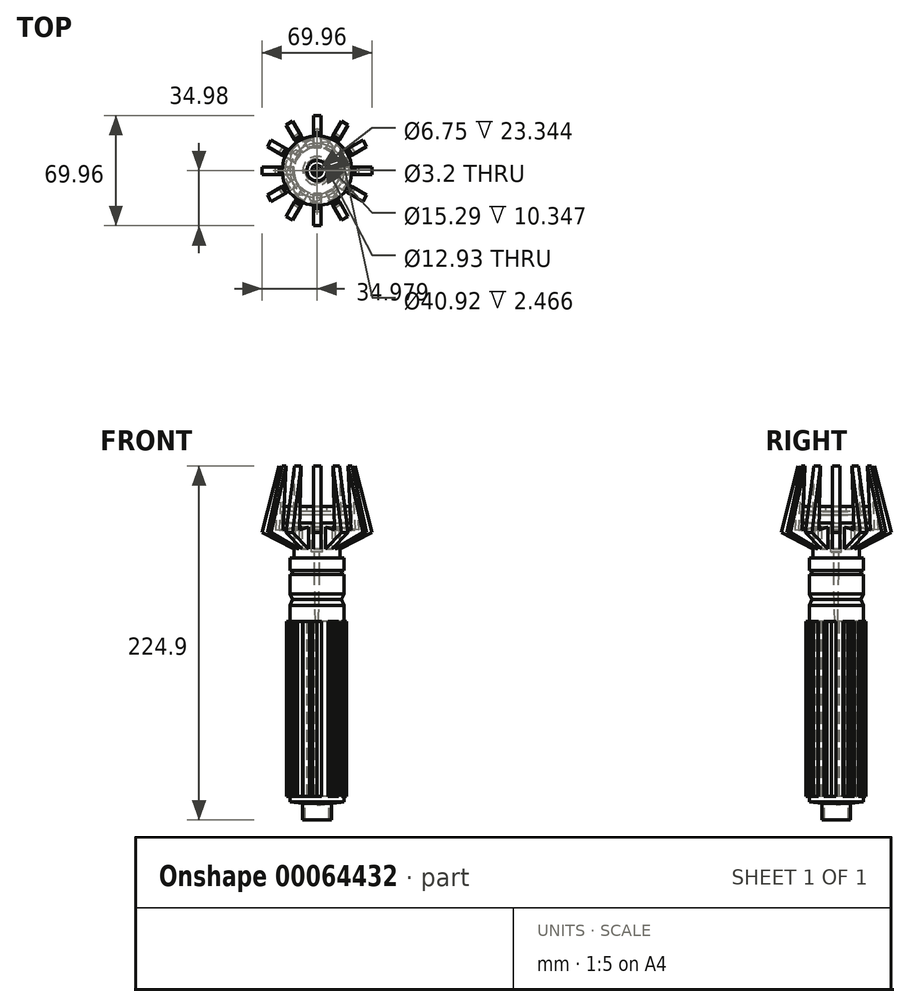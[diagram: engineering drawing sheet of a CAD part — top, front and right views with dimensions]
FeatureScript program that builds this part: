
annotation { "Feature Type Name" : "Feature", "Feature Type Description" : "" }
export const myFeature = defineFeature(function(context is Context, id is Id, definition is map)
    precondition{}
    {
        {
            var Q0;
            Q0=qCreatedBy(makeId("Front.planeOp"),FACE);
            var sketch = newSketch(context, id + "F0", { "sketchPlane" : qUnion([Q0])});
            skLineSegment(sketch, "E0", {"start": v(-15.09, 0) * mm, "end": v(0, 0) * mm});
            skLineSegment(sketch, "E1", {"start": v(-13.85, 0) * mm, "end": v(-13.85, -23.34) * mm});
            skLineSegment(sketch, "E2", {"start": v(-13.85, -23.34) * mm, "end": v(-2.49, -23.34) * mm});
            skLineSegment(sketch, "E3", {"start": v(-2.49, -23.34) * mm, "end": v(-2.49, 0) * mm});
            skLineSegment(sketch, "E4", {"start": v(-13.85, -23.34) * mm, "end": v(-15.62, -23.34) * mm});
            skLineSegment(sketch, "E5", {"start": v(-15.62, -23.34) * mm, "end": v(-15.62, -37.54) * mm});
            skLineSegment(sketch, "E6", {"start": v(-15.62, -37.54) * mm, "end": v(-1.6, -37.54) * mm});
            skLineSegment(sketch, "E7", {"start": v(-1.6, -37.54) * mm, "end": v(-1.6, -35.06) * mm});
            skLineSegment(sketch, "E8", {"start": v(-1.6, -35.06) * mm, "end": v(0, -35.06) * mm});
            skLineSegment(sketch, "E9", {"start": v(0, -35.06) * mm, "end": v(0, -27.25) * mm});
            skLineSegment(sketch, "E10", {"start": v(0, -27.25) * mm, "end": v(-2.49, -27.25) * mm});
            skLineSegment(sketch, "E11", {"start": v(-2.49, -27.25) * mm, "end": v(-2.49, -23.34) * mm});
            skLineSegment(sketch, "E12", {"start": v(0, -37.72) * mm, "end": v(-1.6, -37.54) * mm});
            skLineSegment(sketch, "E13", {"start": v(-17.22, -115.43) * mm, "end": v(0, -115.43) * mm});
            skLineSegment(sketch, "E14", {"start": v(-17.22, -184.16) * mm, "end": v(0, -182.02) * mm});
            skPoint(sketch, "E15.end.orphan", {"position": v(0, -148.72) * mm});
            skPoint(sketch, "E16.start.orphan", {"position": v(0, 9.14) * mm});
            skPoint(sketch, "E17.start.orphan", {"position": v(-2.67, 19.04) * mm});
            skPoint(sketch, "E18.start.orphan", {"position": v(-15.09, 1.93) * mm});
            skLineSegment(sketch, "E19", {"start": v(-9.58, -183.21) * mm, "end": v(-9.58, -193.56) * mm});
            skLineSegment(sketch, "E20", {"start": v(-9.58, -193.56) * mm, "end": v(-8.13, -193.56) * mm});
            skLineSegment(sketch, "E21", {"start": v(-8.13, -193.56) * mm, "end": v(-8.13, -183.03) * mm});
            skLineSegment(sketch, "E22", {"start": v(0, 0) * mm, "end": v(4.91, -4.97) * mm});
            skLineSegment(sketch, "E23", {"start": v(4.91, -4.97) * mm, "end": v(4.91, 5.57) * mm});
            skLineSegment(sketch, "E24", {"start": v(4.91, 5.57) * mm, "end": v(-10.76, 5.57) * mm});
            skLineSegment(sketch, "E25", {"start": v(-10.76, 5.57) * mm, "end": v(-10.76, 2.47) * mm});
            skLineSegment(sketch, "E26", {"start": v(-10.76, 2.47) * mm, "end": v(3.24, 2.47) * mm});
            skLineSegment(sketch, "E27", {"start": v(3.24, 2.47) * mm, "end": v(3.24, 0) * mm});
            skLineSegment(sketch, "E28", {"start": v(3.24, 0) * mm, "end": v(0, 0) * mm});
            skPoint(sketch, "E29.endSnap0", {"position": v(-8.61, -115.43) * mm});
            skPoint(sketch, "E29.end.orphan", {"position": v(-10.3, -115.43) * mm});
            skPoint(sketch, "E30.end.orphan", {"position": v(0, -74.3) * mm});
            skLineSegment(sketch, "E31", {"start": v(-15.62, -37.54) * mm, "end": v(-16.49, -79.81) * mm});
            skLineSegment(sketch, "E32", {"start": v(-16.63, -86.58) * mm, "end": v(-16.49, -79.81) * mm});
            skLineSegment(sketch, "E33", {"start": v(-17.22, -115.43) * mm, "end": v(-17.03, -105.98) * mm});
            skLineSegment(sketch, "E34", {"start": v(-16.63, -86.58) * mm, "end": v(-17.03, -105.98) * mm});
            skLineSegment(sketch, "E35", {"start": v(0, -37.72) * mm, "end": v(0, -50.06) * mm});
            skLineSegment(sketch, "E36", {"start": v(0, -50.06) * mm, "end": v(-1.74, -53.5) * mm});
            skLineSegment(sketch, "E37", {"start": v(-1.74, -53.5) * mm, "end": v(0, -57.28) * mm});
            skLineSegment(sketch, "E38", {"start": v(0, -57.28) * mm, "end": v(0, -115.43) * mm});
            skPoint(sketch, "E39.start.orphan", {"position": v(0, -122.23) * mm});
            skPoint(sketch, "E40.start.orphan", {"position": v(0, -128.68) * mm});
            skPoint(sketch, "E41.start.orphan", {"position": v(0.56, -132.44) * mm});
            skPoint(sketch, "E42.start.orphan", {"position": v(0, -135.5) * mm});
            skPoint(sketch, "E43.start.orphan", {"position": v(0, -141.49) * mm});
            skPoint(sketch, "E44.start.orphan", {"position": v(0, -147) * mm});
            skPoint(sketch, "E45.end.orphan", {"position": v(0, -151.47) * mm});
            skPoint(sketch, "E46.start.orphan", {"position": v(0, -157.22) * mm});
            skPoint(sketch, "E47.start.orphan", {"position": v(0, -162.86) * mm});
            skPoint(sketch, "E48.start.orphan", {"position": v(0, -169.44) * mm});
            skPoint(sketch, "E49.end.orphan", {"position": v(0, -174.84) * mm});
            skPoint(sketch, "E50.start.orphan", {"position": v(0, -180.13) * mm});
            skLineSegment(sketch, "E51.trimOffspring", {"start": v(0, -147) * mm, "end": v(0, -148.72) * mm});
            skPoint(sketch, "E52.end.orphan", {"position": v(-25.8, 0) * mm});
            skLineSegment(sketch, "E53", {"start": v(-15.62, -37.54) * mm, "end": v(-27.2, -82.66) * mm});
            skLineSegment(sketch, "E54", {"start": v(-27.2, -82.66) * mm, "end": v(-17.22, -115.43) * mm});
            skLineSegment(sketch, "E55.trimOffspring", {"start": v(0, -180.13) * mm, "end": v(0, -182.02) * mm});
            skLineSegment(sketch, "E56.trimOffspring", {"start": v(0, -148.72) * mm, "end": v(0, -151.47) * mm});
            skLineSegment(sketch, "E57", {"start": v(-17.22, -115.43) * mm, "end": v(-17.22, -184.16) * mm});
            skLineSegment(sketch, "E58", {"start": v(0, -115.43) * mm, "end": v(0, -180.13) * mm});
            skPoint(sketch, "E59.end.orphan", {"position": v(0, -114.59) * mm});
            skSolve(sketch);
        }
        {
            var Q0;
            Q0=makeQuery(id+"F0.imprint","IMPRINT",FACE,{"disambiguationData":[TD([[makeQuery(id+"F0.imprint","IMPRINT",EDGE,{"derivedFrom":sQuery(id+"F0.wireOp",EDGE,"E22")}),1.0]])]});
            var Q1;
            {var subQ0=sQuery(id+"F0.wireOp",EDGE,"E1");Q1=makeQuery(id+"F0.imprint","IMPRINT",FACE,{"disambiguationData":[TD([[makeQuery(id+"F0.imprint","IMPRINT",EDGE,{"derivedFrom":subQ0}),1.0]])]});}
            var Q2;
            {var subQ0=sQuery(id+"F0.wireOp",EDGE,"E19");Q2=makeQuery(id+"F0.imprint","IMPRINT",FACE,{"disambiguationData":[TD([[makeQuery(id+"F0.imprint","IMPRINT",EDGE,{"derivedFrom":subQ0}),1.0]])]});}
            var Q3;
            Q3=makeQuery(id+"F0.imprint","IMPRINT",FACE,{"disambiguationData":[TD([[makeQuery(id+"F0.imprint","IMPRINT",EDGE,{"derivedFrom":sQuery(id+"F0.wireOp",EDGE,"E2")}),-1.0]])]});
            var Q4;
            {var subQ6=sQuery(id+"F0.wireOp",EDGE,"E13");Q4=makeQuery(id+"F0.imprint","IMPRINT",FACE,{"disambiguationData":[TD([[makeQuery(id+"F0.imprint","IMPRINT",EDGE,{"derivedFrom":subQ6}),-1.0]])]});}
            var Q5;
            Q5=makeQuery(id+"F0.imprint","IMPRINT",FACE,{"disambiguationData":[TD([[makeQuery(id+"F0.imprint","IMPRINT",EDGE,{"derivedFrom":sQuery(id+"F0.wireOp",EDGE,"E6")}),-1.0]])]});
            var Q6;
            Q6=sQuery(id+"F0.wireOp",EDGE,"E57");
            revolve(context, id + "F1", {"entities" : qUnion([Q0, Q1, Q2, Q3, Q4, Q5]), "axis" : qUnion([Q6]), "revolveType" : RevolveType.FULL});
        }
        {
            var Q0;
            Q0=qCreatedBy(makeId("Front.planeOp"),FACE);
            var sketch = newSketch(context, id + "F2", { "sketchPlane" : qUnion([Q0])});
            skLineSegment(sketch, "E60", {"start": v(-31.91, -21.3) * mm, "end": v(-52.2, -10.94) * mm});
            skLineSegment(sketch, "E61", {"start": v(-52.2, -10.94) * mm, "end": v(-41.44, 31.34) * mm});
            skLineSegment(sketch, "E62", {"start": v(-41.44, 31.34) * mm, "end": v(-43.6, -9.36) * mm});
            skLineSegment(sketch, "E63", {"start": v(-43.6, -9.36) * mm, "end": v(-31.9, -7.63) * mm});
            skLineSegment(sketch, "E64", {"start": v(-31.9, -7.63) * mm, "end": v(-31.91, -21.3) * mm});
            skSolve(sketch);
        }
        {
            var Q0;
            Q0=qCreatedBy(makeId("Top.planeOp"),FACE);
            cPlane(context, id + "F3", {"entities" : qUnion([Q0]), "cplaneType" : CPlaneType.OFFSET, "offset" : 127 * mm, "oppositeDirection" : true, "width" : 152.4 * mm, "height" : 152.4 * mm});
        }
        {
            var Q0;
            Q0=qCreatedBy(id+"F3.planeOp",FACE);
            var sketch = newSketch(context, id + "F4", { "sketchPlane" : qUnion([Q0])});
            skCircle(sketch, "E65", {"center": v(-17.35, 0) * mm, "radius": 17.24 * mm});
            skLineSegment(sketch, "E66", {"start": v(-22.02, -16.6) * mm, "end": v(-22.02, -17.9) * mm});
            skLineSegment(sketch, "E67", {"start": v(-22.02, -17.9) * mm, "end": v(-20, -19.22) * mm});
            skLineSegment(sketch, "E68", {"start": v(-20, -19.22) * mm, "end": v(-17.22, -19.22) * mm});
            skLineSegment(sketch, "E69", {"start": v(-17.22, -19.22) * mm, "end": v(-14.42, -17.81) * mm});
            skLineSegment(sketch, "E70", {"start": v(-14.42, -17.81) * mm, "end": v(-14.42, -16.99) * mm});
            skLineSegment(sketch, "E71.1.1", {"start": v(-3.65, -11.76) * mm, "end": v(-4.18, -11.13) * mm});
            skLineSegment(sketch, "E71.1.2", {"start": v(-4.9, -14.64) * mm, "end": v(-3.65, -11.76) * mm});
            skLineSegment(sketch, "E71.1.3", {"start": v(-7.02, -16.42) * mm, "end": v(-4.9, -14.64) * mm});
            skLineSegment(sketch, "E71.1.4", {"start": v(-9.41, -16.72) * mm, "end": v(-7.02, -16.42) * mm});
            skLineSegment(sketch, "E71.1.5", {"start": v(-10.26, -15.71) * mm, "end": v(-9.41, -16.72) * mm});
            skLineSegment(sketch, "E71.2.1", {"start": v(0.7, -0.2) * mm, "end": v(-0.11, -0.06) * mm});
            skLineSegment(sketch, "E71.2.2", {"start": v(1.6, -3.2) * mm, "end": v(0.7, -0.2) * mm});
            skLineSegment(sketch, "E71.2.3", {"start": v(1.12, -5.94) * mm, "end": v(1.6, -3.2) * mm});
            skLineSegment(sketch, "E71.2.4", {"start": v(-0.52, -7.7) * mm, "end": v(1.12, -5.94) * mm});
            skLineSegment(sketch, "E71.2.5", {"start": v(-1.82, -7.48) * mm, "end": v(-0.52, -7.7) * mm});
            skLineSegment(sketch, "E71.3.1", {"start": v(-3.39, 11.45) * mm, "end": v(-4.1, 11.03) * mm});
            skLineSegment(sketch, "E71.3.2", {"start": v(-0.77, 9.72) * mm, "end": v(-3.39, 11.45) * mm});
            skLineSegment(sketch, "E71.3.3", {"start": v(0.62, 7.32) * mm, "end": v(-0.77, 9.72) * mm});
            skLineSegment(sketch, "E71.3.4", {"start": v(0.5, 4.9) * mm, "end": v(0.62, 7.32) * mm});
            skLineSegment(sketch, "E71.3.5", {"start": v(-0.64, 4.25) * mm, "end": v(0.5, 4.9) * mm});
            skLineSegment(sketch, "E71.4.1", {"start": v(-14.01, 17.74) * mm, "end": v(-14.3, 16.96) * mm});
            skLineSegment(sketch, "E71.4.2", {"start": v(-10.9, 18.1) * mm, "end": v(-14.01, 17.74) * mm});
            skLineSegment(sketch, "E71.4.3", {"start": v(-8.3, 17.15) * mm, "end": v(-10.9, 18.1) * mm});
            skLineSegment(sketch, "E71.4.4", {"start": v(-6.84, 15.23) * mm, "end": v(-8.3, 17.15) * mm});
            skLineSegment(sketch, "E71.4.5", {"start": v(-7.28, 14) * mm, "end": v(-6.84, 15.23) * mm});
            skLineSegment(sketch, "E71.5.1", {"start": v(-26.2, 15.74) * mm, "end": v(-25.91, 14.96) * mm});
            skLineSegment(sketch, "E71.5.2", {"start": v(-24.04, 18.01) * mm, "end": v(-26.2, 15.74) * mm});
            skLineSegment(sketch, "E71.5.3", {"start": v(-21.44, 18.96) * mm, "end": v(-24.04, 18.01) * mm});
            skLineSegment(sketch, "E71.5.4", {"start": v(-19.09, 18.43) * mm, "end": v(-21.44, 18.96) * mm});
            skLineSegment(sketch, "E71.5.5", {"start": v(-18.64, 17.19) * mm, "end": v(-19.09, 18.43) * mm});
            skLineSegment(sketch, "E71.6.1", {"start": v(-34.24, 6.37) * mm, "end": v(-33.53, 5.95) * mm});
            skLineSegment(sketch, "E71.6.2", {"start": v(-34.06, 9.5) * mm, "end": v(-34.24, 6.37) * mm});
            skLineSegment(sketch, "E71.6.3", {"start": v(-32.67, 11.9) * mm, "end": v(-34.06, 9.5) * mm});
            skLineSegment(sketch, "E71.6.4", {"start": v(-30.52, 13) * mm, "end": v(-32.67, 11.9) * mm});
            skLineSegment(sketch, "E71.6.5", {"start": v(-29.38, 12.34) * mm, "end": v(-30.52, 13) * mm});
            skLineSegment(sketch, "E71.7.1", {"start": v(-34.38, -5.98) * mm, "end": v(-33.57, -5.84) * mm});
            skLineSegment(sketch, "E71.7.2", {"start": v(-36.25, -3.47) * mm, "end": v(-34.38, -5.98) * mm});
            skLineSegment(sketch, "E71.7.3", {"start": v(-36.73, -0.73) * mm, "end": v(-36.25, -3.47) * mm});
            skLineSegment(sketch, "E71.7.4", {"start": v(-35.8, 1.49) * mm, "end": v(-36.73, -0.73) * mm});
            skLineSegment(sketch, "E71.7.5", {"start": v(-34.5, 1.72) * mm, "end": v(-35.8, 1.49) * mm});
            skLineSegment(sketch, "E71.8.1", {"start": v(-26.55, -15.53) * mm, "end": v(-26.02, -14.9) * mm});
            skLineSegment(sketch, "E71.8.2", {"start": v(-29.6, -14.8) * mm, "end": v(-26.55, -15.53) * mm});
            skLineSegment(sketch, "E71.8.3", {"start": v(-31.73, -13.02) * mm, "end": v(-29.6, -14.8) * mm});
            skLineSegment(sketch, "E71.8.4", {"start": v(-32.44, -10.72) * mm, "end": v(-31.73, -13.02) * mm});
            skLineSegment(sketch, "E71.8.5", {"start": v(-31.6, -9.7) * mm, "end": v(-32.44, -10.72) * mm});
            skSolve(sketch);
        }
        {
            var Q0;
            Q0 = qSketchRegion(id + "F4", true);
            extrude(context, id + "F5", {"entities" : qUnion([Q0]), "operationType" : NewBodyOperationType.ADD, "depth" : 59.53 * mm, "hasSecondDirection" : true, "secondDirectionOppositeDirection" : true, "secondDirectionDepth" : 51.47 * mm});
        }
        {
            var Q0;
            Q0=qCreatedBy(makeId("Top.planeOp"),FACE);
            cPlane(context, id + "F6", {"entities" : qUnion([Q0]), "cplaneType" : CPlaneType.OFFSET, "offset" : 12.7 * mm, "oppositeDirection" : true, "width" : 152.4 * mm, "height" : 152.4 * mm});
        }
        {
            var Q0;
            Q0 = qSketchRegion(id + "F2", true);
            extrude(context, id + "F7", {"entities" : qUnion([Q0]), "depth" : 2.4 * mm, "hasSecondDirection" : true, "secondDirectionOppositeDirection" : true, "secondDirectionDepth" : 2.4 * mm});
        }
        {
            var Q0;
            Q0=makeQuery(id+"F7.opExtrude","SWEPT_BODY",BODY,{"disambiguationData":[OSD([sQuery(id+"F2.wireOp",EDGE,"E60"),sQuery(id+"F2.wireOp",EDGE,"E61"),sQuery(id+"F2.wireOp",EDGE,"E62"),sQuery(id+"F2.wireOp",EDGE,"E63"),sQuery(id+"F2.wireOp",EDGE,"E64")])]});
            var Q1;
            Q1=makeQuery(id+"F1.opRevolve","SWEPT_FACE",FACE,{"disambiguationData":[OSD([sQuery(id+"F0.wireOp",EDGE,"E23")])]});
            circularPattern(context, id + "F8", {"entities" : qUnion([Q0]), "axis" : qUnion([Q1]), "angle" : 30 * degree, "instanceCount" : 12});
        }
    });
